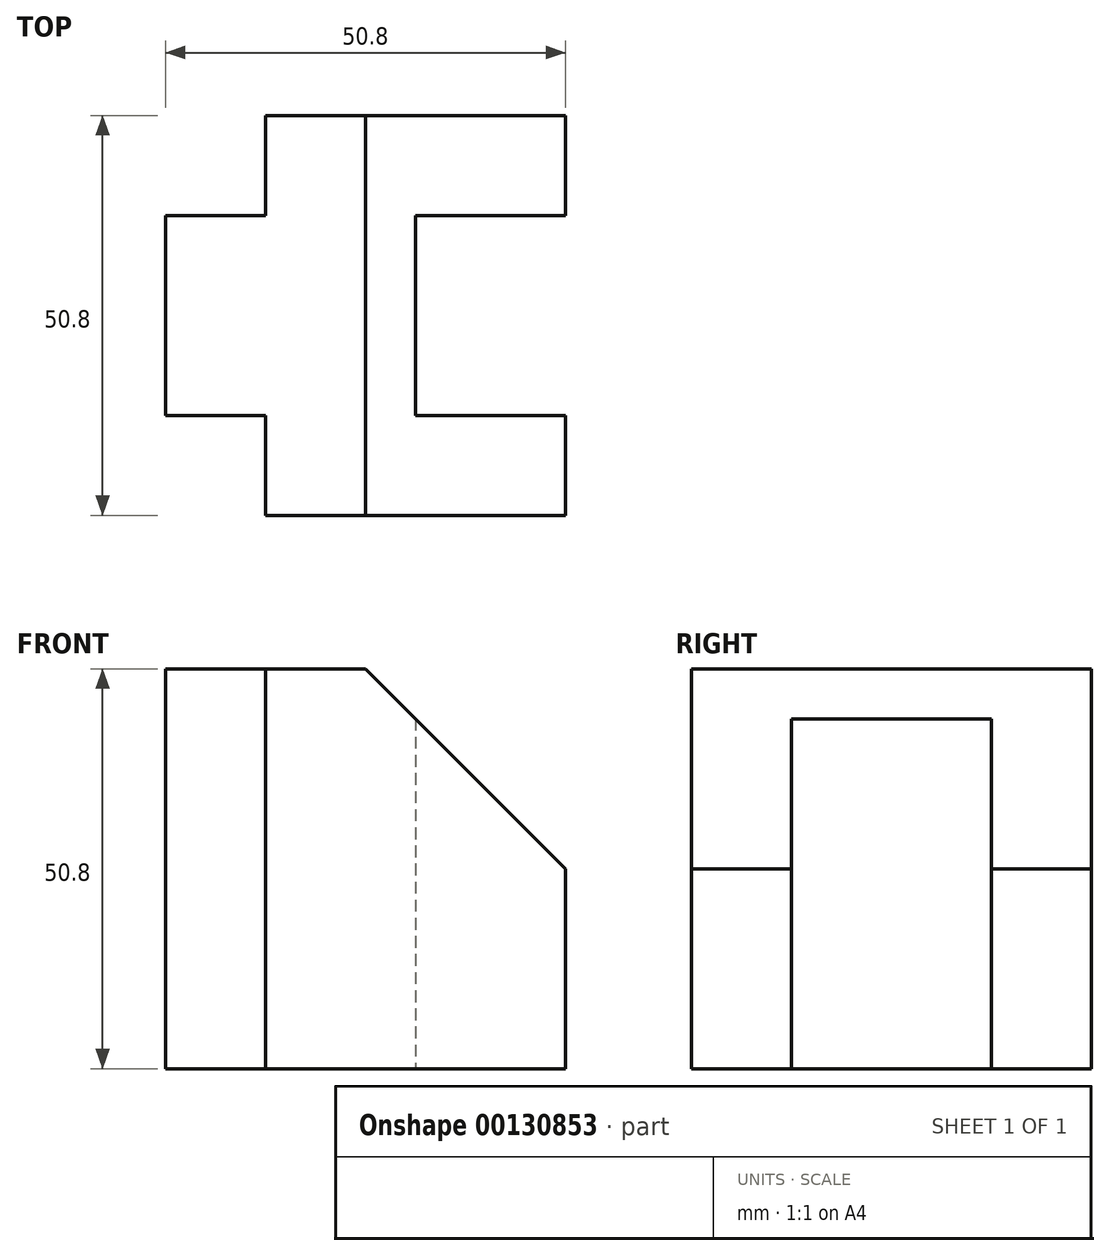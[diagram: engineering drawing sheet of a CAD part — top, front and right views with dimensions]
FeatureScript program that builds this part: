
annotation { "Feature Type Name" : "Feature", "Feature Type Description" : "" }
export const myFeature = defineFeature(function(context is Context, id is Id, definition is map)
    precondition{}
    {
        {
            var Q0;
            Q0=qCreatedBy(makeId("Front.planeOp"),FACE);
            var sketch = newSketch(context, id + "F0", { "sketchPlane" : qUnion([Q0])});
            skLineSegment(sketch, "E0", {"start": v(0, 0) * mm, "end": v(50.8, 0) * mm});
            skLineSegment(sketch, "E1", {"start": v(50.8, 0) * mm, "end": v(50.8, 25.4) * mm});
            skLineSegment(sketch, "E2", {"start": v(50.8, 25.4) * mm, "end": v(25.4, 50.8) * mm});
            skLineSegment(sketch, "E3", {"start": v(25.4, 50.8) * mm, "end": v(0, 50.8) * mm});
            skLineSegment(sketch, "E4", {"start": v(0, 50.8) * mm, "end": v(0, 0) * mm});
            skLineSegment(sketch, "E5", {"start": v(0, 0) * mm, "end": v(12.7, 0) * mm});
            skLineSegment(sketch, "E6", {"start": v(12.7, 0) * mm, "end": v(12.7, 50.8) * mm});
            skSolve(sketch);
        }
        {
            var Q0;
            Q0 = qSketchRegion(id + "F0", true);
            extrude(context, id + "F1", {"entities" : qUnion([Q0]), "oppositeDirection" : true, "depth" : 50.8 * mm});
        }
        {
            var Q0;
            Q0=makeQuery(id+"F1.opExtrude","SWEPT_FACE",FACE,{"disambiguationData":[OSD([sQuery(id+"F0.wireOp",EDGE,"E3")])]});
            var sketch = newSketch(context, id + "F2", { "sketchPlane" : qUnion([Q0])});
            skLineSegment(sketch, "E7", {"start": v(0, 0) * mm, "end": v(12.7, 0) * mm});
            skLineSegment(sketch, "E8", {"start": v(12.7, 0) * mm, "end": v(12.7, 12.7) * mm});
            skLineSegment(sketch, "E9", {"start": v(12.7, 12.7) * mm, "end": v(0, 12.7) * mm});
            skLineSegment(sketch, "E10", {"start": v(0, 12.7) * mm, "end": v(0, 38.1) * mm});
            skLineSegment(sketch, "E11", {"start": v(0, 38.1) * mm, "end": v(12.7, 38.1) * mm});
            skLineSegment(sketch, "E12", {"start": v(12.7, 38.1) * mm, "end": v(12.7, 50.8) * mm});
            skSolve(sketch);
        }
        {
            var Q0;
            {var subQ0=sQuery(id+"F2.wireOp",EDGE,"E11");Q0=makeQuery(id+"F2.imprint","IMPRINT",FACE,{"disambiguationData":[TD([[makeQuery(id+"F2.imprint","IMPRINT",EDGE,{"derivedFrom":subQ0}),1.0]])]});}
            var Q1;
            {var subQ0=sQuery(id+"F2.wireOp",EDGE,"E7");Q1=makeQuery(id+"F2.imprint","IMPRINT",FACE,{"disambiguationData":[TD([[makeQuery(id+"F2.imprint","IMPRINT",EDGE,{"derivedFrom":subQ0}),-1.0]])]});}
            extrude(context, id + "F3", {"entities" : qUnion([Q0, Q1]), "operationType" : NewBodyOperationType.REMOVE, "oppositeDirection" : true, "depth" : 62.73 * mm});
        }
        {
            var Q0;
            Q0=makeQuery(id+"F1.opExtrude","SWEPT_FACE",FACE,{"disambiguationData":[OSD([sQuery(id+"F0.wireOp",EDGE,"E0"),sQuery(id+"F0.wireOp",EDGE,"E5")])]});
            var sketch = newSketch(context, id + "F4", { "sketchPlane" : qUnion([Q0])});
            skLineSegment(sketch, "E13", {"start": v(50.8, -12.7) * mm, "end": v(31.75, -12.7) * mm});
            skLineSegment(sketch, "E14", {"start": v(31.75, -12.7) * mm, "end": v(31.75, -38.1) * mm});
            skLineSegment(sketch, "E15", {"start": v(31.75, -38.1) * mm, "end": v(50.8, -38.1) * mm});
            skSolve(sketch);
        }
        {
            var Q0;
            {var subQ0=sQuery(id+"F4.wireOp",EDGE,"E13");Q0=makeQuery(id+"F4.imprint","IMPRINT",FACE,{"disambiguationData":[TD([[makeQuery(id+"F4.imprint","IMPRINT",EDGE,{"derivedFrom":subQ0}),1.0]])]});}
            extrude(context, id + "F5", {"entities" : qUnion([Q0]), "operationType" : NewBodyOperationType.REMOVE, "oppositeDirection" : true, "depth" : 90.92 * mm});
        }
    });
